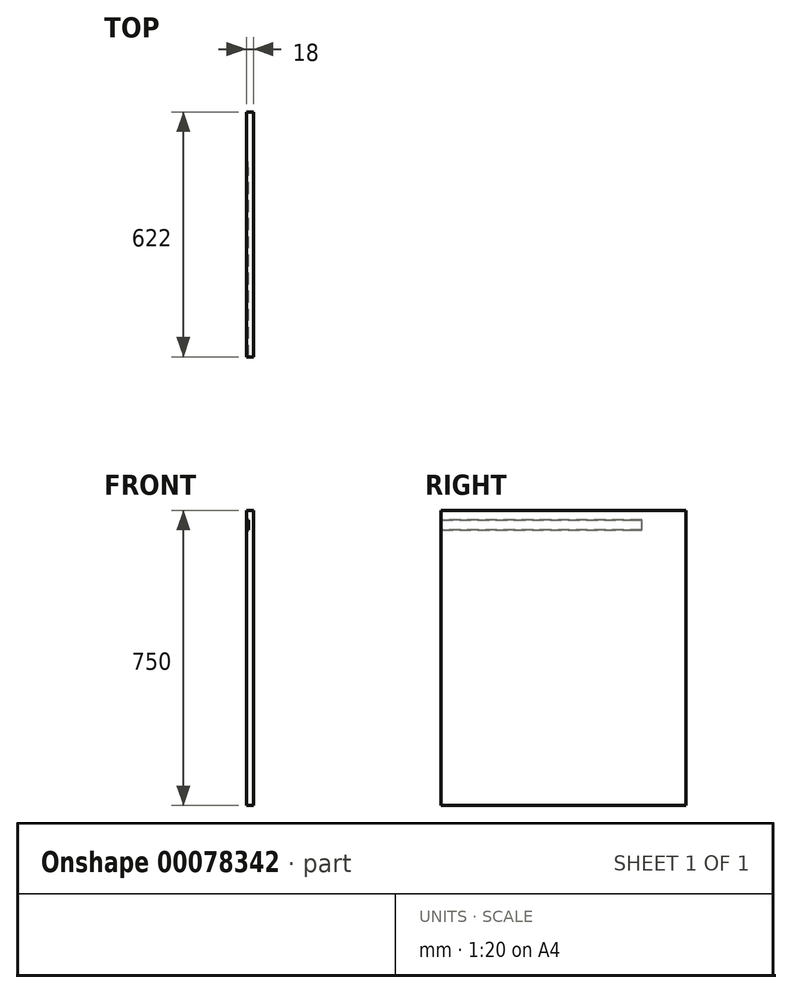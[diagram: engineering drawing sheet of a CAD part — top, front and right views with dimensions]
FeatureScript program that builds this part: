
annotation { "Feature Type Name" : "Feature", "Feature Type Description" : "" }
export const myFeature = defineFeature(function(context is Context, id is Id, definition is map)
    precondition{}
    {
        {
            var Q0;
            Q0=qCreatedBy(makeId("Right.planeOp"),FACE);
            var sketch = newSketch(context, id + "F0", { "sketchPlane" : qUnion([Q0])});
            skLineSegment(sketch, "E0.bottom", {"start": v(-308.23, 451.19) * mm, "end": v(313.77, 451.19) * mm});
            skLineSegment(sketch, "E0.top", {"start": v(-308.23, -298.81) * mm, "end": v(313.77, -298.81) * mm});
            skLineSegment(sketch, "E0.left", {"start": v(-308.23, 451.19) * mm, "end": v(-308.23, -298.81) * mm});
            skLineSegment(sketch, "E0.right", {"start": v(313.77, 451.19) * mm, "end": v(313.77, -298.81) * mm});
            skSolve(sketch);
        }
        {
            var Q0;
            Q0=makeQuery(id+"F0.imprint","IMPRINT",FACE,{"disambiguationData":[TD([[makeQuery(id+"F0.imprint","IMPRINT",EDGE,{"derivedFrom":sQuery(id+"F0.wireOp",EDGE,"E0.bottom")}),-1.0]])]});
            extrude(context, id + "F1", {"entities" : qUnion([Q0]), "depth" : 18 * mm});
        }
        {
            var Q0;
            Q0=makeQuery(id+"F1.opExtrude","SWEPT_FACE",FACE,{"disambiguationData":[OSD([sQuery(id+"F0.wireOp",EDGE,"E0.bottom")])]});
            cPlane(context, id + "F2", {"entities" : qUnion([Q0]), "cplaneType" : CPlaneType.OFFSET, "offset" : 25 * mm, "oppositeDirection" : true, "width" : 150 * mm, "height" : 150 * mm});
        }
        {
            var Q0;
            Q0=qCreatedBy(id+"F2.planeOp",FACE);
            var sketch = newSketch(context, id + "F3", { "sketchPlane" : qUnion([Q0])});
            skLineSegment(sketch, "E1", {"start": v(5, -308.23) * mm, "end": v(5, 171.77) * mm});
            skPoint(sketch, "E2.visualSharp", {"position": v(5, 203.4) * mm});
            skArc(sketch, "E3", {"start": v(5, 171.77) * mm, "mid": v(3.74, 186.97) * mm, "end": v(0, 201.77) * mm});
            skLineSegment(sketch, "E4", {"start": v(0, 201.77) * mm, "end": v(0, -308.23) * mm});
            skLineSegment(sketch, "E5", {"start": v(0, -308.23) * mm, "end": v(5, -308.23) * mm});
            skSolve(sketch);
        }
        {
            var Q0;
            {var subQ0=sQuery(id+"F3.wireOp",EDGE,"E1");Q0=makeQuery(id+"F3.imprint","IMPRINT",FACE,{"disambiguationData":[TD([[makeQuery(id+"F3.imprint","IMPRINT",EDGE,{"derivedFrom":subQ0}),1.0]])]});}
            extrude(context, id + "F4", {"entities" : qUnion([Q0]), "operationType" : NewBodyOperationType.REMOVE, "oppositeDirection" : true, "depth" : 25 * mm});
        }
    });
